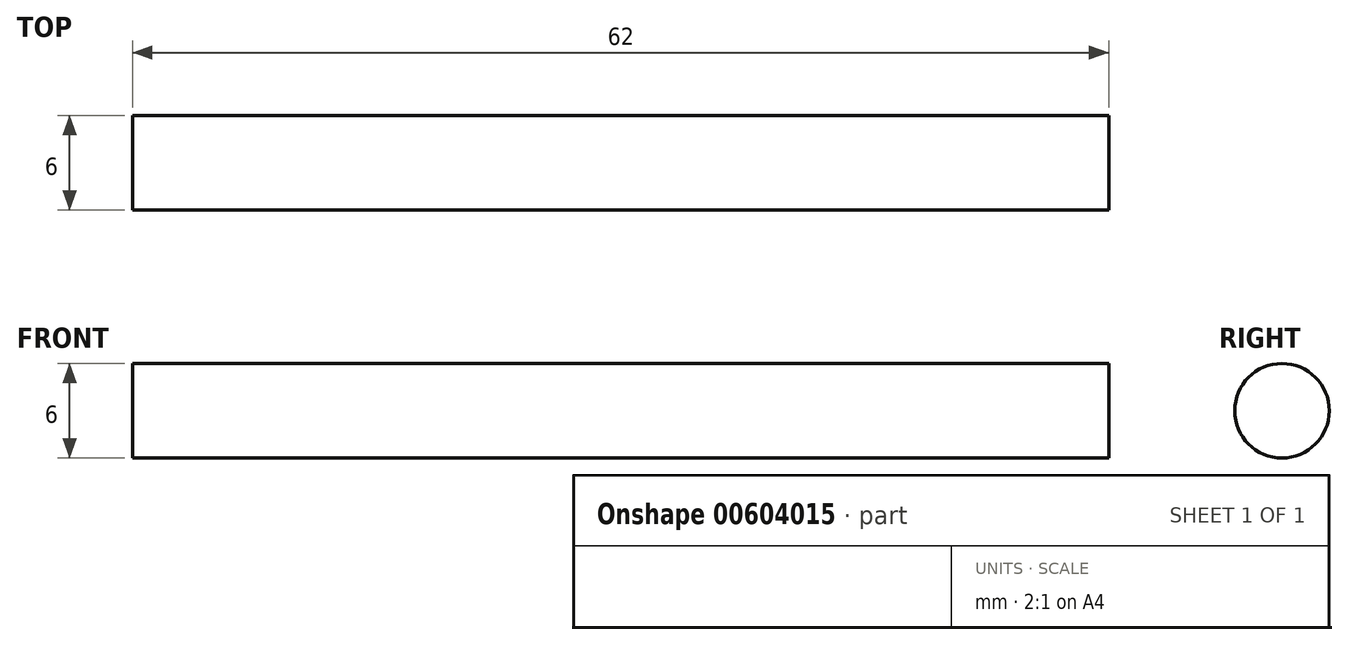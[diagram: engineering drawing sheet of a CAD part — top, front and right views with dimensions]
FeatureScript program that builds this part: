
annotation { "Feature Type Name" : "Feature", "Feature Type Description" : "" }
export const myFeature = defineFeature(function(context is Context, id is Id, definition is map)
    precondition{}
    {
        {
            var Q0;
            Q0=qCreatedBy(makeId("Front.planeOp"),FACE);
            var sketch = newSketch(context, id + "F0", { "sketchPlane" : qUnion([Q0])});
            skLineSegment(sketch, "E0.bottom", {"start": v(-31, 1.5) * mm, "end": v(31, 1.5) * mm});
            skLineSegment(sketch, "E0.top", {"start": v(-31, -1.5) * mm, "end": v(31, -1.5) * mm});
            skLineSegment(sketch, "E0.left", {"start": v(-31, 1.5) * mm, "end": v(-31, -1.5) * mm});
            skLineSegment(sketch, "E0.right", {"start": v(31, 1.5) * mm, "end": v(31, -1.5) * mm});
            skPoint(sketch, "E0.middle", {"position": v(0, 0) * mm});
            skSolve(sketch);
        }
        {
            var Q0;
            Q0=makeQuery(id+"F0.imprint","IMPRINT",FACE,{"disambiguationData":[TD([[makeQuery(id+"F0.imprint","IMPRINT",EDGE,{"derivedFrom":sQuery(id+"F0.wireOp",EDGE,"E0.bottom")}),-1.0]])]});
            var Q1;
            Q1=sQuery(id+"F0.wireOp",EDGE,"E0.top");
            revolve(context, id + "F1", {"entities" : qUnion([Q0]), "axis" : qUnion([Q1]), "revolveType" : RevolveType.FULL});
        }
    });
